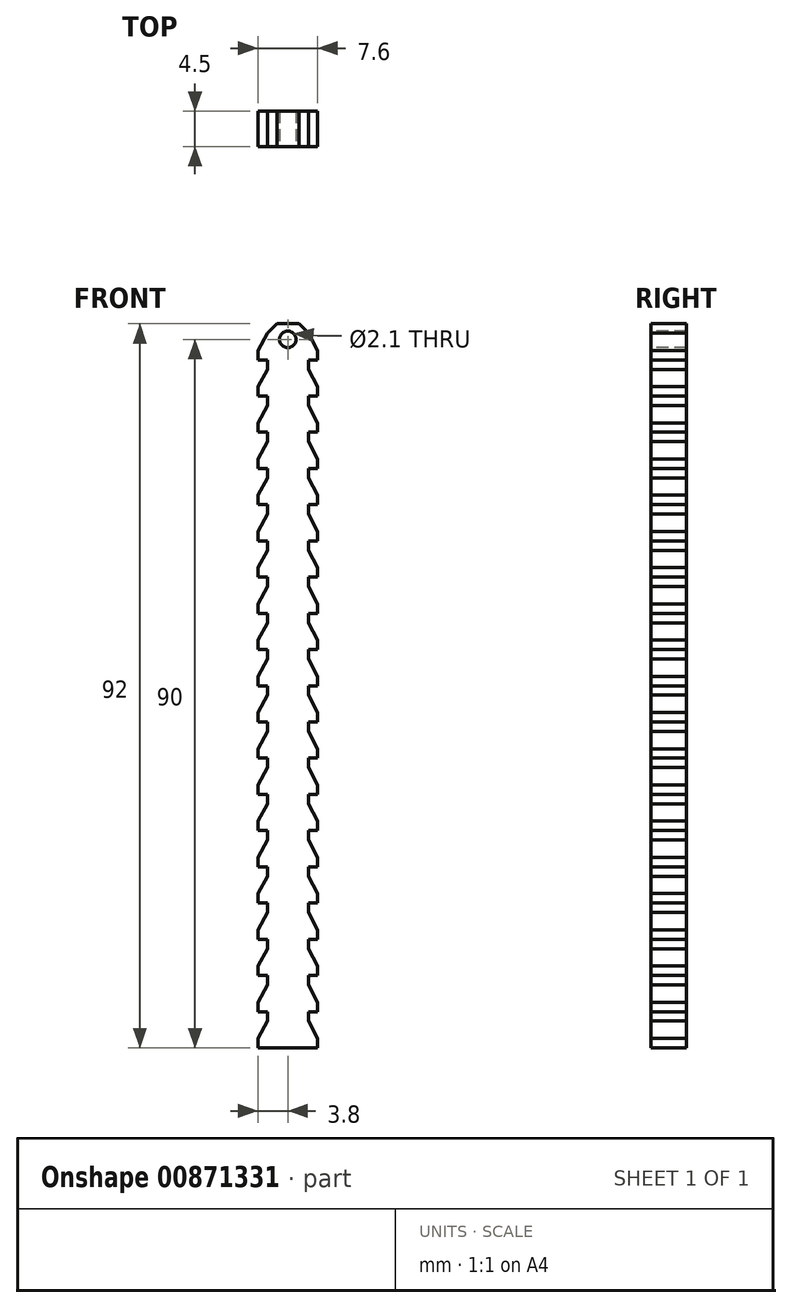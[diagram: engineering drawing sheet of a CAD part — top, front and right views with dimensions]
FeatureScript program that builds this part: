
annotation { "Feature Type Name" : "Feature", "Feature Type Description" : "" }
export const myFeature = defineFeature(function(context is Context, id is Id, definition is map)
    precondition{}
    {
        {
            var Q0;
            Q0=qCreatedBy(makeId("Front.planeOp"),FACE);
            var sketch = newSketch(context, id + "F0", { "sketchPlane" : qUnion([Q0])});
            skLineSegment(sketch, "E0", {"start": v(-3.8, 0) * mm, "end": v(-3.8, 1.2) * mm});
            skLineSegment(sketch, "E1", {"start": v(-3.8, 1.2) * mm, "end": v(-2.6, 3.4) * mm});
            skLineSegment(sketch, "E2", {"start": v(-2.6, 3.4) * mm, "end": v(-2.6, 4.6) * mm});
            skLineSegment(sketch, "E3", {"start": v(-2.6, 4.6) * mm, "end": v(-3.8, 4.6) * mm});
            skLineSegment(sketch, "E4", {"start": v(-3.8, 4.6) * mm, "end": v(-3.8, 5.8) * mm});
            skLineSegment(sketch, "E5", {"start": v(-3.8, 5.8) * mm, "end": v(-2.6, 8) * mm});
            skLineSegment(sketch, "E6", {"start": v(-3.8, 0) * mm, "end": v(-2.6, 0) * mm});
            skLineSegment(sketch, "E7.MirrorCS", {"start": v(2.6, 4.6) * mm, "end": v(3.8, 4.6) * mm});
            skLineSegment(sketch, "E8.MirrorCS", {"start": v(3.8, 4.6) * mm, "end": v(3.8, 5.8) * mm});
            skLineSegment(sketch, "E9.MirrorCS", {"start": v(2.6, 3.4) * mm, "end": v(2.6, 4.6) * mm});
            skLineSegment(sketch, "E10.MirrorCS", {"start": v(3.8, 0) * mm, "end": v(3.8, 1.2) * mm});
            skLineSegment(sketch, "E11.MirrorCS", {"start": v(3.8, 0) * mm, "end": v(2.6, 0) * mm});
            skLineSegment(sketch, "E12.MirrorCS", {"start": v(3.8, 5.8) * mm, "end": v(2.6, 8) * mm});
            skLineSegment(sketch, "E13.MirrorCS", {"start": v(3.8, 1.2) * mm, "end": v(2.6, 3.4) * mm});
            skLineSegment(sketch, "E14", {"start": v(-2.6, 8) * mm, "end": v(-2.6, 9.2) * mm});
            skLineSegment(sketch, "E15", {"start": v(2.6, 8) * mm, "end": v(2.6, 9.2) * mm});
            skLineSegment(sketch, "E16.0.1.0", {"start": v(-2.6, 12.6) * mm, "end": v(-2.6, 13.8) * mm});
            skLineSegment(sketch, "E16.0.1.1", {"start": v(-2.6, 17.2) * mm, "end": v(-2.6, 18.4) * mm});
            skLineSegment(sketch, "E16.0.1.2", {"start": v(-3.8, 10.4) * mm, "end": v(-2.6, 12.6) * mm});
            skLineSegment(sketch, "E16.0.1.3", {"start": v(2.6, 12.6) * mm, "end": v(2.6, 13.8) * mm});
            skLineSegment(sketch, "E16.0.1.4", {"start": v(2.6, 13.8) * mm, "end": v(3.8, 13.8) * mm});
            skLineSegment(sketch, "E16.0.1.5", {"start": v(2.6, 17.2) * mm, "end": v(2.6, 18.4) * mm});
            skLineSegment(sketch, "E16.0.1.6", {"start": v(-3.8, 9.2) * mm, "end": v(-2.6, 9.2) * mm});
            skLineSegment(sketch, "E16.0.1.7", {"start": v(-2.6, 13.8) * mm, "end": v(-3.8, 13.8) * mm});
            skLineSegment(sketch, "E16.0.1.8", {"start": v(-3.8, 15) * mm, "end": v(-2.6, 17.2) * mm});
            skLineSegment(sketch, "E16.0.1.9", {"start": v(-3.8, 13.8) * mm, "end": v(-3.8, 15) * mm});
            skLineSegment(sketch, "E16.0.1.10", {"start": v(3.8, 10.4) * mm, "end": v(2.6, 12.6) * mm});
            skLineSegment(sketch, "E16.0.1.11", {"start": v(3.8, 9.2) * mm, "end": v(3.8, 10.4) * mm});
            skLineSegment(sketch, "E16.0.1.12", {"start": v(-3.8, 9.2) * mm, "end": v(-3.8, 10.4) * mm});
            skLineSegment(sketch, "E16.0.1.13", {"start": v(3.8, 9.2) * mm, "end": v(2.6, 9.2) * mm});
            skLineSegment(sketch, "E16.0.1.14", {"start": v(3.8, 13.8) * mm, "end": v(3.8, 15) * mm});
            skLineSegment(sketch, "E16.0.1.15", {"start": v(3.8, 15) * mm, "end": v(2.6, 17.2) * mm});
            skLineSegment(sketch, "E16.0.2.0", {"start": v(-2.6, 21.8) * mm, "end": v(-2.6, 23) * mm});
            skLineSegment(sketch, "E16.0.2.1", {"start": v(-2.6, 26.4) * mm, "end": v(-2.6, 27.6) * mm});
            skLineSegment(sketch, "E16.0.2.2", {"start": v(-3.8, 19.6) * mm, "end": v(-2.6, 21.8) * mm});
            skLineSegment(sketch, "E16.0.2.3", {"start": v(2.6, 21.8) * mm, "end": v(2.6, 23) * mm});
            skLineSegment(sketch, "E16.0.2.4", {"start": v(2.6, 23) * mm, "end": v(3.8, 23) * mm});
            skLineSegment(sketch, "E16.0.2.5", {"start": v(2.6, 26.4) * mm, "end": v(2.6, 27.6) * mm});
            skLineSegment(sketch, "E16.0.2.6", {"start": v(-3.8, 18.4) * mm, "end": v(-2.6, 18.4) * mm});
            skLineSegment(sketch, "E16.0.2.7", {"start": v(-2.6, 23) * mm, "end": v(-3.8, 23) * mm});
            skLineSegment(sketch, "E16.0.2.8", {"start": v(-3.8, 24.2) * mm, "end": v(-2.6, 26.4) * mm});
            skLineSegment(sketch, "E16.0.2.9", {"start": v(-3.8, 23) * mm, "end": v(-3.8, 24.2) * mm});
            skLineSegment(sketch, "E16.0.2.10", {"start": v(3.8, 19.6) * mm, "end": v(2.6, 21.8) * mm});
            skLineSegment(sketch, "E16.0.2.11", {"start": v(3.8, 18.4) * mm, "end": v(3.8, 19.6) * mm});
            skLineSegment(sketch, "E16.0.2.12", {"start": v(-3.8, 18.4) * mm, "end": v(-3.8, 19.6) * mm});
            skLineSegment(sketch, "E16.0.2.13", {"start": v(3.8, 18.4) * mm, "end": v(2.6, 18.4) * mm});
            skLineSegment(sketch, "E16.0.2.14", {"start": v(3.8, 23) * mm, "end": v(3.8, 24.2) * mm});
            skLineSegment(sketch, "E16.0.2.15", {"start": v(3.8, 24.2) * mm, "end": v(2.6, 26.4) * mm});
            skLineSegment(sketch, "E16.0.3.0", {"start": v(-2.6, 31) * mm, "end": v(-2.6, 32.2) * mm});
            skLineSegment(sketch, "E16.0.3.1", {"start": v(-2.6, 35.6) * mm, "end": v(-2.6, 36.8) * mm});
            skLineSegment(sketch, "E16.0.3.2", {"start": v(-3.8, 28.8) * mm, "end": v(-2.6, 31) * mm});
            skLineSegment(sketch, "E16.0.3.3", {"start": v(2.6, 31) * mm, "end": v(2.6, 32.2) * mm});
            skLineSegment(sketch, "E16.0.3.4", {"start": v(2.6, 32.2) * mm, "end": v(3.8, 32.2) * mm});
            skLineSegment(sketch, "E16.0.3.5", {"start": v(2.6, 35.6) * mm, "end": v(2.6, 36.8) * mm});
            skLineSegment(sketch, "E16.0.3.6", {"start": v(-3.8, 27.6) * mm, "end": v(-2.6, 27.6) * mm});
            skLineSegment(sketch, "E16.0.3.7", {"start": v(-2.6, 32.2) * mm, "end": v(-3.8, 32.2) * mm});
            skLineSegment(sketch, "E16.0.3.8", {"start": v(-3.8, 33.4) * mm, "end": v(-2.6, 35.6) * mm});
            skLineSegment(sketch, "E16.0.3.9", {"start": v(-3.8, 32.2) * mm, "end": v(-3.8, 33.4) * mm});
            skLineSegment(sketch, "E16.0.3.10", {"start": v(3.8, 28.8) * mm, "end": v(2.6, 31) * mm});
            skLineSegment(sketch, "E16.0.3.11", {"start": v(3.8, 27.6) * mm, "end": v(3.8, 28.8) * mm});
            skLineSegment(sketch, "E16.0.3.12", {"start": v(-3.8, 27.6) * mm, "end": v(-3.8, 28.8) * mm});
            skLineSegment(sketch, "E16.0.3.13", {"start": v(3.8, 27.6) * mm, "end": v(2.6, 27.6) * mm});
            skLineSegment(sketch, "E16.0.3.14", {"start": v(3.8, 32.2) * mm, "end": v(3.8, 33.4) * mm});
            skLineSegment(sketch, "E16.0.3.15", {"start": v(3.8, 33.4) * mm, "end": v(2.6, 35.6) * mm});
            skLineSegment(sketch, "E16.0.4.0", {"start": v(-2.6, 40.2) * mm, "end": v(-2.6, 41.4) * mm});
            skLineSegment(sketch, "E16.0.4.1", {"start": v(-2.6, 44.8) * mm, "end": v(-2.6, 46) * mm});
            skLineSegment(sketch, "E16.0.4.2", {"start": v(-3.8, 38) * mm, "end": v(-2.6, 40.2) * mm});
            skLineSegment(sketch, "E16.0.4.3", {"start": v(2.6, 40.2) * mm, "end": v(2.6, 41.4) * mm});
            skLineSegment(sketch, "E16.0.4.4", {"start": v(2.6, 41.4) * mm, "end": v(3.8, 41.4) * mm});
            skLineSegment(sketch, "E16.0.4.5", {"start": v(2.6, 44.8) * mm, "end": v(2.6, 46) * mm});
            skLineSegment(sketch, "E16.0.4.6", {"start": v(-3.8, 36.8) * mm, "end": v(-2.6, 36.8) * mm});
            skLineSegment(sketch, "E16.0.4.7", {"start": v(-2.6, 41.4) * mm, "end": v(-3.8, 41.4) * mm});
            skLineSegment(sketch, "E16.0.4.8", {"start": v(-3.8, 42.6) * mm, "end": v(-2.6, 44.8) * mm});
            skLineSegment(sketch, "E16.0.4.9", {"start": v(-3.8, 41.4) * mm, "end": v(-3.8, 42.6) * mm});
            skLineSegment(sketch, "E16.0.4.10", {"start": v(3.8, 38) * mm, "end": v(2.6, 40.2) * mm});
            skLineSegment(sketch, "E16.0.4.11", {"start": v(3.8, 36.8) * mm, "end": v(3.8, 38) * mm});
            skLineSegment(sketch, "E16.0.4.12", {"start": v(-3.8, 36.8) * mm, "end": v(-3.8, 38) * mm});
            skLineSegment(sketch, "E16.0.4.13", {"start": v(3.8, 36.8) * mm, "end": v(2.6, 36.8) * mm});
            skLineSegment(sketch, "E16.0.4.14", {"start": v(3.8, 41.4) * mm, "end": v(3.8, 42.6) * mm});
            skLineSegment(sketch, "E16.0.4.15", {"start": v(3.8, 42.6) * mm, "end": v(2.6, 44.8) * mm});
            skLineSegment(sketch, "E16.0.5.0", {"start": v(-2.6, 49.4) * mm, "end": v(-2.6, 50.6) * mm});
            skLineSegment(sketch, "E16.0.5.1", {"start": v(-2.6, 54) * mm, "end": v(-2.6, 55.2) * mm});
            skLineSegment(sketch, "E16.0.5.2", {"start": v(-3.8, 47.2) * mm, "end": v(-2.6, 49.4) * mm});
            skLineSegment(sketch, "E16.0.5.3", {"start": v(2.6, 49.4) * mm, "end": v(2.6, 50.6) * mm});
            skLineSegment(sketch, "E16.0.5.4", {"start": v(2.6, 50.6) * mm, "end": v(3.8, 50.6) * mm});
            skLineSegment(sketch, "E16.0.5.5", {"start": v(2.6, 54) * mm, "end": v(2.6, 55.2) * mm});
            skLineSegment(sketch, "E16.0.5.6", {"start": v(-3.8, 46) * mm, "end": v(-2.6, 46) * mm});
            skLineSegment(sketch, "E16.0.5.7", {"start": v(-2.6, 50.6) * mm, "end": v(-3.8, 50.6) * mm});
            skLineSegment(sketch, "E16.0.5.8", {"start": v(-3.8, 51.8) * mm, "end": v(-2.6, 54) * mm});
            skLineSegment(sketch, "E16.0.5.9", {"start": v(-3.8, 50.6) * mm, "end": v(-3.8, 51.8) * mm});
            skLineSegment(sketch, "E16.0.5.10", {"start": v(3.8, 47.2) * mm, "end": v(2.6, 49.4) * mm});
            skLineSegment(sketch, "E16.0.5.11", {"start": v(3.8, 46) * mm, "end": v(3.8, 47.2) * mm});
            skLineSegment(sketch, "E16.0.5.12", {"start": v(-3.8, 46) * mm, "end": v(-3.8, 47.2) * mm});
            skLineSegment(sketch, "E16.0.5.13", {"start": v(3.8, 46) * mm, "end": v(2.6, 46) * mm});
            skLineSegment(sketch, "E16.0.5.14", {"start": v(3.8, 50.6) * mm, "end": v(3.8, 51.8) * mm});
            skLineSegment(sketch, "E16.0.5.15", {"start": v(3.8, 51.8) * mm, "end": v(2.6, 54) * mm});
            skLineSegment(sketch, "E16.0.6.0", {"start": v(-2.6, 58.6) * mm, "end": v(-2.6, 59.8) * mm});
            skLineSegment(sketch, "E16.0.6.1", {"start": v(-2.6, 63.2) * mm, "end": v(-2.6, 64.4) * mm});
            skLineSegment(sketch, "E16.0.6.2", {"start": v(-3.8, 56.4) * mm, "end": v(-2.6, 58.6) * mm});
            skLineSegment(sketch, "E16.0.6.3", {"start": v(2.6, 58.6) * mm, "end": v(2.6, 59.8) * mm});
            skLineSegment(sketch, "E16.0.6.4", {"start": v(2.6, 59.8) * mm, "end": v(3.8, 59.8) * mm});
            skLineSegment(sketch, "E16.0.6.5", {"start": v(2.6, 63.2) * mm, "end": v(2.6, 64.4) * mm});
            skLineSegment(sketch, "E16.0.6.6", {"start": v(-3.8, 55.2) * mm, "end": v(-2.6, 55.2) * mm});
            skLineSegment(sketch, "E16.0.6.7", {"start": v(-2.6, 59.8) * mm, "end": v(-3.8, 59.8) * mm});
            skLineSegment(sketch, "E16.0.6.8", {"start": v(-3.8, 61) * mm, "end": v(-2.6, 63.2) * mm});
            skLineSegment(sketch, "E16.0.6.9", {"start": v(-3.8, 59.8) * mm, "end": v(-3.8, 61) * mm});
            skLineSegment(sketch, "E16.0.6.10", {"start": v(3.8, 56.4) * mm, "end": v(2.6, 58.6) * mm});
            skLineSegment(sketch, "E16.0.6.11", {"start": v(3.8, 55.2) * mm, "end": v(3.8, 56.4) * mm});
            skLineSegment(sketch, "E16.0.6.12", {"start": v(-3.8, 55.2) * mm, "end": v(-3.8, 56.4) * mm});
            skLineSegment(sketch, "E16.0.6.13", {"start": v(3.8, 55.2) * mm, "end": v(2.6, 55.2) * mm});
            skLineSegment(sketch, "E16.0.6.14", {"start": v(3.8, 59.8) * mm, "end": v(3.8, 61) * mm});
            skLineSegment(sketch, "E16.0.6.15", {"start": v(3.8, 61) * mm, "end": v(2.6, 63.2) * mm});
            skLineSegment(sketch, "E16.0.7.0", {"start": v(-2.6, 67.8) * mm, "end": v(-2.6, 69) * mm});
            skLineSegment(sketch, "E16.0.7.1", {"start": v(-2.6, 72.4) * mm, "end": v(-2.6, 73.6) * mm});
            skLineSegment(sketch, "E16.0.7.2", {"start": v(-3.8, 65.6) * mm, "end": v(-2.6, 67.8) * mm});
            skLineSegment(sketch, "E16.0.7.3", {"start": v(2.6, 67.8) * mm, "end": v(2.6, 69) * mm});
            skLineSegment(sketch, "E16.0.7.4", {"start": v(2.6, 69) * mm, "end": v(3.8, 69) * mm});
            skLineSegment(sketch, "E16.0.7.5", {"start": v(2.6, 72.4) * mm, "end": v(2.6, 73.6) * mm});
            skLineSegment(sketch, "E16.0.7.6", {"start": v(-3.8, 64.4) * mm, "end": v(-2.6, 64.4) * mm});
            skLineSegment(sketch, "E16.0.7.7", {"start": v(-2.6, 69) * mm, "end": v(-3.8, 69) * mm});
            skLineSegment(sketch, "E16.0.7.8", {"start": v(-3.8, 70.2) * mm, "end": v(-2.6, 72.4) * mm});
            skLineSegment(sketch, "E16.0.7.9", {"start": v(-3.8, 69) * mm, "end": v(-3.8, 70.2) * mm});
            skLineSegment(sketch, "E16.0.7.10", {"start": v(3.8, 65.6) * mm, "end": v(2.6, 67.8) * mm});
            skLineSegment(sketch, "E16.0.7.11", {"start": v(3.8, 64.4) * mm, "end": v(3.8, 65.6) * mm});
            skLineSegment(sketch, "E16.0.7.12", {"start": v(-3.8, 64.4) * mm, "end": v(-3.8, 65.6) * mm});
            skLineSegment(sketch, "E16.0.7.13", {"start": v(3.8, 64.4) * mm, "end": v(2.6, 64.4) * mm});
            skLineSegment(sketch, "E16.0.7.14", {"start": v(3.8, 69) * mm, "end": v(3.8, 70.2) * mm});
            skLineSegment(sketch, "E16.0.7.15", {"start": v(3.8, 70.2) * mm, "end": v(2.6, 72.4) * mm});
            skLineSegment(sketch, "E16.0.8.0", {"start": v(-2.6, 77) * mm, "end": v(-2.6, 78.2) * mm});
            skLineSegment(sketch, "E16.0.8.1", {"start": v(-2.6, 81.6) * mm, "end": v(-2.6, 82.8) * mm});
            skLineSegment(sketch, "E16.0.8.2", {"start": v(-3.8, 74.8) * mm, "end": v(-2.6, 77) * mm});
            skLineSegment(sketch, "E16.0.8.3", {"start": v(2.6, 77) * mm, "end": v(2.6, 78.2) * mm});
            skLineSegment(sketch, "E16.0.8.4", {"start": v(2.6, 78.2) * mm, "end": v(3.8, 78.2) * mm});
            skLineSegment(sketch, "E16.0.8.5", {"start": v(2.6, 81.6) * mm, "end": v(2.6, 82.8) * mm});
            skLineSegment(sketch, "E16.0.8.6", {"start": v(-3.8, 73.6) * mm, "end": v(-2.6, 73.6) * mm});
            skLineSegment(sketch, "E16.0.8.7", {"start": v(-2.6, 78.2) * mm, "end": v(-3.8, 78.2) * mm});
            skLineSegment(sketch, "E16.0.8.8", {"start": v(-3.8, 79.4) * mm, "end": v(-2.6, 81.6) * mm});
            skLineSegment(sketch, "E16.0.8.9", {"start": v(-3.8, 78.2) * mm, "end": v(-3.8, 79.4) * mm});
            skLineSegment(sketch, "E16.0.8.10", {"start": v(3.8, 74.8) * mm, "end": v(2.6, 77) * mm});
            skLineSegment(sketch, "E16.0.8.11", {"start": v(3.8, 73.6) * mm, "end": v(3.8, 74.8) * mm});
            skLineSegment(sketch, "E16.0.8.12", {"start": v(-3.8, 73.6) * mm, "end": v(-3.8, 74.8) * mm});
            skLineSegment(sketch, "E16.0.8.13", {"start": v(3.8, 73.6) * mm, "end": v(2.6, 73.6) * mm});
            skLineSegment(sketch, "E16.0.8.14", {"start": v(3.8, 78.2) * mm, "end": v(3.8, 79.4) * mm});
            skLineSegment(sketch, "E16.0.8.15", {"start": v(3.8, 79.4) * mm, "end": v(2.6, 81.6) * mm});
            skLineSegment(sketch, "E16.0.9.0", {"start": v(-2.6, 86.2) * mm, "end": v(-2.6, 87.4) * mm});
            skLineSegment(sketch, "E16.0.9.1", {"start": v(-2.6, 90.8) * mm, "end": v(-2.6, 92) * mm});
            skLineSegment(sketch, "E16.0.9.2", {"start": v(-3.8, 84) * mm, "end": v(-2.6, 86.2) * mm});
            skLineSegment(sketch, "E16.0.9.3", {"start": v(2.6, 86.2) * mm, "end": v(2.6, 87.4) * mm});
            skLineSegment(sketch, "E16.0.9.4", {"start": v(2.6, 87.4) * mm, "end": v(3.8, 87.4) * mm});
            skLineSegment(sketch, "E16.0.9.5", {"start": v(2.6, 90.8) * mm, "end": v(2.6, 92) * mm});
            skLineSegment(sketch, "E16.0.9.6", {"start": v(-3.8, 82.8) * mm, "end": v(-2.6, 82.8) * mm});
            skLineSegment(sketch, "E16.0.9.7", {"start": v(-2.6, 87.4) * mm, "end": v(-3.8, 87.4) * mm});
            skLineSegment(sketch, "E16.0.9.8", {"start": v(-3.8, 88.6) * mm, "end": v(-2.6, 90.8) * mm});
            skLineSegment(sketch, "E16.0.9.9", {"start": v(-3.8, 87.4) * mm, "end": v(-3.8, 88.6) * mm});
            skLineSegment(sketch, "E16.0.9.10", {"start": v(3.8, 84) * mm, "end": v(2.6, 86.2) * mm});
            skLineSegment(sketch, "E16.0.9.11", {"start": v(3.8, 82.8) * mm, "end": v(3.8, 84) * mm});
            skLineSegment(sketch, "E16.0.9.12", {"start": v(-3.8, 82.8) * mm, "end": v(-3.8, 84) * mm});
            skLineSegment(sketch, "E16.0.9.13", {"start": v(3.8, 82.8) * mm, "end": v(2.6, 82.8) * mm});
            skLineSegment(sketch, "E16.0.9.14", {"start": v(3.8, 87.4) * mm, "end": v(3.8, 88.6) * mm});
            skLineSegment(sketch, "E16.0.9.15", {"start": v(3.8, 88.6) * mm, "end": v(2.6, 90.8) * mm});
            skLineSegment(sketch, "E16.direction1", {"start": v(-3.8, 0) * mm, "end": v(21, 0) * mm, "construction": true});
            skLineSegment(sketch, "E16.direction2", {"start": v(-3.8, 0) * mm, "end": v(-3.8, 9.2) * mm, "construction": true});
            skLineSegment(sketch, "E17", {"start": v(-2.6, 0) * mm, "end": v(2.6, 0) * mm});
            skLineSegment(sketch, "E18", {"start": v(-2.6, 92) * mm, "end": v(2.6, 92) * mm});
            skSolve(sketch);
        }
        {
            var Q0;
            Q0=makeQuery(id+"F0.imprint","IMPRINT",FACE,{"disambiguationData":[TD([[makeQuery(id+"F0.imprint","IMPRINT",EDGE,{"derivedFrom":sQuery(id+"F0.wireOp",EDGE,"E0")}),-1.0]])]});
            extrude(context, id + "F1", {"entities" : qUnion([Q0]), "depth" : 4.5 * mm, "offsetDistance" : 25 * mm});
        }
        {
            var Q0;
            Q0=makeQuery(id+"F1.opExtrude","SWEPT_EDGE",EDGE,{"disambiguationData":[OSD([sQuery(id+"F0.wireOp",EDGE,"E16.0.9.5"),sQuery(id+"F0.wireOp",EDGE,"E18")])]});
            var Q1;
            Q1=makeQuery(id+"F1.opExtrude","SWEPT_EDGE",EDGE,{"disambiguationData":[OSD([sQuery(id+"F0.wireOp",EDGE,"E16.0.9.1"),sQuery(id+"F0.wireOp",EDGE,"E18")])]});
            chamfer(context, id + "F2", {"entities" : qUnion([Q0, Q1]), "width" : 1.2 * mm, "tangentPropagation" : true});
        }
        {
            var Q0;
            Q0=makeQuery(id+"F1.opExtrude","CAP_FACE",FACE,{"disambiguationData":[OSD([sQuery(id+"F0.wireOp",EDGE,"E0"),sQuery(id+"F0.wireOp",EDGE,"E1"),sQuery(id+"F0.wireOp",EDGE,"E2"),sQuery(id+"F0.wireOp",EDGE,"E3"),sQuery(id+"F0.wireOp",EDGE,"E4"),sQuery(id+"F0.wireOp",EDGE,"E5"),sQuery(id+"F0.wireOp",EDGE,"E6"),sQuery(id+"F0.wireOp",EDGE,"E7.MirrorCS"),sQuery(id+"F0.wireOp",EDGE,"E8.MirrorCS"),sQuery(id+"F0.wireOp",EDGE,"E9.MirrorCS"),sQuery(id+"F0.wireOp",EDGE,"E10.MirrorCS"),sQuery(id+"F0.wireOp",EDGE,"E11.MirrorCS"),sQuery(id+"F0.wireOp",EDGE,"E12.MirrorCS"),sQuery(id+"F0.wireOp",EDGE,"E13.MirrorCS"),sQuery(id+"F0.wireOp",EDGE,"E14"),sQuery(id+"F0.wireOp",EDGE,"E15"),sQuery(id+"F0.wireOp",EDGE,"E16.0.1.0"),sQuery(id+"F0.wireOp",EDGE,"E16.0.1.1"),sQuery(id+"F0.wireOp",EDGE,"E16.0.1.2"),sQuery(id+"F0.wireOp",EDGE,"E16.0.1.3"),sQuery(id+"F0.wireOp",EDGE,"E16.0.1.4"),sQuery(id+"F0.wireOp",EDGE,"E16.0.1.5"),sQuery(id+"F0.wireOp",EDGE,"E16.0.1.6"),sQuery(id+"F0.wireOp",EDGE,"E16.0.1.7"),sQuery(id+"F0.wireOp",EDGE,"E16.0.1.8"),sQuery(id+"F0.wireOp",EDGE,"E16.0.1.9"),sQuery(id+"F0.wireOp",EDGE,"E16.0.1.10"),sQuery(id+"F0.wireOp",EDGE,"E16.0.1.11"),sQuery(id+"F0.wireOp",EDGE,"E16.0.1.12"),sQuery(id+"F0.wireOp",EDGE,"E16.0.1.13"),sQuery(id+"F0.wireOp",EDGE,"E16.0.1.14"),sQuery(id+"F0.wireOp",EDGE,"E16.0.1.15"),sQuery(id+"F0.wireOp",EDGE,"E16.0.2.0"),sQuery(id+"F0.wireOp",EDGE,"E16.0.2.1"),sQuery(id+"F0.wireOp",EDGE,"E16.0.2.2"),sQuery(id+"F0.wireOp",EDGE,"E16.0.2.3"),sQuery(id+"F0.wireOp",EDGE,"E16.0.2.4"),sQuery(id+"F0.wireOp",EDGE,"E16.0.2.5"),sQuery(id+"F0.wireOp",EDGE,"E16.0.2.6"),sQuery(id+"F0.wireOp",EDGE,"E16.0.2.7"),sQuery(id+"F0.wireOp",EDGE,"E16.0.2.8"),sQuery(id+"F0.wireOp",EDGE,"E16.0.2.9"),sQuery(id+"F0.wireOp",EDGE,"E16.0.2.10"),sQuery(id+"F0.wireOp",EDGE,"E16.0.2.11"),sQuery(id+"F0.wireOp",EDGE,"E16.0.2.12"),sQuery(id+"F0.wireOp",EDGE,"E16.0.2.13"),sQuery(id+"F0.wireOp",EDGE,"E16.0.2.14"),sQuery(id+"F0.wireOp",EDGE,"E16.0.2.15"),sQuery(id+"F0.wireOp",EDGE,"E16.0.3.0"),sQuery(id+"F0.wireOp",EDGE,"E16.0.3.1"),sQuery(id+"F0.wireOp",EDGE,"E16.0.3.2"),sQuery(id+"F0.wireOp",EDGE,"E16.0.3.3"),sQuery(id+"F0.wireOp",EDGE,"E16.0.3.4"),sQuery(id+"F0.wireOp",EDGE,"E16.0.3.5"),sQuery(id+"F0.wireOp",EDGE,"E16.0.3.6"),sQuery(id+"F0.wireOp",EDGE,"E16.0.3.7"),sQuery(id+"F0.wireOp",EDGE,"E16.0.3.8"),sQuery(id+"F0.wireOp",EDGE,"E16.0.3.9"),sQuery(id+"F0.wireOp",EDGE,"E16.0.3.10"),sQuery(id+"F0.wireOp",EDGE,"E16.0.3.11"),sQuery(id+"F0.wireOp",EDGE,"E16.0.3.12"),sQuery(id+"F0.wireOp",EDGE,"E16.0.3.13"),sQuery(id+"F0.wireOp",EDGE,"E16.0.3.14"),sQuery(id+"F0.wireOp",EDGE,"E16.0.3.15"),sQuery(id+"F0.wireOp",EDGE,"E16.0.4.0"),sQuery(id+"F0.wireOp",EDGE,"E16.0.4.1"),sQuery(id+"F0.wireOp",EDGE,"E16.0.4.2"),sQuery(id+"F0.wireOp",EDGE,"E16.0.4.3"),sQuery(id+"F0.wireOp",EDGE,"E16.0.4.4"),sQuery(id+"F0.wireOp",EDGE,"E16.0.4.5"),sQuery(id+"F0.wireOp",EDGE,"E16.0.4.6"),sQuery(id+"F0.wireOp",EDGE,"E16.0.4.7"),sQuery(id+"F0.wireOp",EDGE,"E16.0.4.8"),sQuery(id+"F0.wireOp",EDGE,"E16.0.4.9"),sQuery(id+"F0.wireOp",EDGE,"E16.0.4.10"),sQuery(id+"F0.wireOp",EDGE,"E16.0.4.11"),sQuery(id+"F0.wireOp",EDGE,"E16.0.4.12"),sQuery(id+"F0.wireOp",EDGE,"E16.0.4.13"),sQuery(id+"F0.wireOp",EDGE,"E16.0.4.14"),sQuery(id+"F0.wireOp",EDGE,"E16.0.4.15"),sQuery(id+"F0.wireOp",EDGE,"E16.0.5.0"),sQuery(id+"F0.wireOp",EDGE,"E16.0.5.1"),sQuery(id+"F0.wireOp",EDGE,"E16.0.5.2"),sQuery(id+"F0.wireOp",EDGE,"E16.0.5.3"),sQuery(id+"F0.wireOp",EDGE,"E16.0.5.4"),sQuery(id+"F0.wireOp",EDGE,"E16.0.5.5"),sQuery(id+"F0.wireOp",EDGE,"E16.0.5.6"),sQuery(id+"F0.wireOp",EDGE,"E16.0.5.7"),sQuery(id+"F0.wireOp",EDGE,"E16.0.5.8"),sQuery(id+"F0.wireOp",EDGE,"E16.0.5.9"),sQuery(id+"F0.wireOp",EDGE,"E16.0.5.10"),sQuery(id+"F0.wireOp",EDGE,"E16.0.5.11"),sQuery(id+"F0.wireOp",EDGE,"E16.0.5.12"),sQuery(id+"F0.wireOp",EDGE,"E16.0.5.13"),sQuery(id+"F0.wireOp",EDGE,"E16.0.5.14"),sQuery(id+"F0.wireOp",EDGE,"E16.0.5.15"),sQuery(id+"F0.wireOp",EDGE,"E16.0.6.0"),sQuery(id+"F0.wireOp",EDGE,"E16.0.6.1"),sQuery(id+"F0.wireOp",EDGE,"E16.0.6.2"),sQuery(id+"F0.wireOp",EDGE,"E16.0.6.3"),sQuery(id+"F0.wireOp",EDGE,"E16.0.6.4"),sQuery(id+"F0.wireOp",EDGE,"E16.0.6.5"),sQuery(id+"F0.wireOp",EDGE,"E16.0.6.6"),sQuery(id+"F0.wireOp",EDGE,"E16.0.6.7"),sQuery(id+"F0.wireOp",EDGE,"E16.0.6.8"),sQuery(id+"F0.wireOp",EDGE,"E16.0.6.9"),sQuery(id+"F0.wireOp",EDGE,"E16.0.6.10"),sQuery(id+"F0.wireOp",EDGE,"E16.0.6.11"),sQuery(id+"F0.wireOp",EDGE,"E16.0.6.12"),sQuery(id+"F0.wireOp",EDGE,"E16.0.6.13"),sQuery(id+"F0.wireOp",EDGE,"E16.0.6.14"),sQuery(id+"F0.wireOp",EDGE,"E16.0.6.15"),sQuery(id+"F0.wireOp",EDGE,"E16.0.7.0"),sQuery(id+"F0.wireOp",EDGE,"E16.0.7.1"),sQuery(id+"F0.wireOp",EDGE,"E16.0.7.2"),sQuery(id+"F0.wireOp",EDGE,"E16.0.7.3"),sQuery(id+"F0.wireOp",EDGE,"E16.0.7.4"),sQuery(id+"F0.wireOp",EDGE,"E16.0.7.5"),sQuery(id+"F0.wireOp",EDGE,"E16.0.7.6"),sQuery(id+"F0.wireOp",EDGE,"E16.0.7.7"),sQuery(id+"F0.wireOp",EDGE,"E16.0.7.8"),sQuery(id+"F0.wireOp",EDGE,"E16.0.7.9"),sQuery(id+"F0.wireOp",EDGE,"E16.0.7.10"),sQuery(id+"F0.wireOp",EDGE,"E16.0.7.11"),sQuery(id+"F0.wireOp",EDGE,"E16.0.7.12"),sQuery(id+"F0.wireOp",EDGE,"E16.0.7.13"),sQuery(id+"F0.wireOp",EDGE,"E16.0.7.14"),sQuery(id+"F0.wireOp",EDGE,"E16.0.7.15"),sQuery(id+"F0.wireOp",EDGE,"E16.0.8.0"),sQuery(id+"F0.wireOp",EDGE,"E16.0.8.1"),sQuery(id+"F0.wireOp",EDGE,"E16.0.8.2"),sQuery(id+"F0.wireOp",EDGE,"E16.0.8.3"),sQuery(id+"F0.wireOp",EDGE,"E16.0.8.4"),sQuery(id+"F0.wireOp",EDGE,"E16.0.8.5"),sQuery(id+"F0.wireOp",EDGE,"E16.0.8.6"),sQuery(id+"F0.wireOp",EDGE,"E16.0.8.7"),sQuery(id+"F0.wireOp",EDGE,"E16.0.8.8"),sQuery(id+"F0.wireOp",EDGE,"E16.0.8.9"),sQuery(id+"F0.wireOp",EDGE,"E16.0.8.10"),sQuery(id+"F0.wireOp",EDGE,"E16.0.8.11"),sQuery(id+"F0.wireOp",EDGE,"E16.0.8.12"),sQuery(id+"F0.wireOp",EDGE,"E16.0.8.13"),sQuery(id+"F0.wireOp",EDGE,"E16.0.8.14"),sQuery(id+"F0.wireOp",EDGE,"E16.0.8.15"),sQuery(id+"F0.wireOp",EDGE,"E16.0.9.0"),sQuery(id+"F0.wireOp",EDGE,"E16.0.9.1"),sQuery(id+"F0.wireOp",EDGE,"E16.0.9.2"),sQuery(id+"F0.wireOp",EDGE,"E16.0.9.3"),sQuery(id+"F0.wireOp",EDGE,"E16.0.9.4"),sQuery(id+"F0.wireOp",EDGE,"E16.0.9.5"),sQuery(id+"F0.wireOp",EDGE,"E16.0.9.6"),sQuery(id+"F0.wireOp",EDGE,"E16.0.9.7"),sQuery(id+"F0.wireOp",EDGE,"E16.0.9.8"),sQuery(id+"F0.wireOp",EDGE,"E16.0.9.9"),sQuery(id+"F0.wireOp",EDGE,"E16.0.9.10"),sQuery(id+"F0.wireOp",EDGE,"E16.0.9.11"),sQuery(id+"F0.wireOp",EDGE,"E16.0.9.12"),sQuery(id+"F0.wireOp",EDGE,"E16.0.9.13"),sQuery(id+"F0.wireOp",EDGE,"E16.0.9.14"),sQuery(id+"F0.wireOp",EDGE,"E16.0.9.15"),sQuery(id+"F0.wireOp",EDGE,"E17"),sQuery(id+"F0.wireOp",EDGE,"E18")])],"isStart":false});
            var sketch = newSketch(context, id + "F3", { "sketchPlane" : qUnion([Q0])});
            skCircle(sketch, "E19", {"center": v(0, 28.3) * mm, "radius": 0.5 * mm});
            skCircle(sketch, "E20", {"center": v(0, 90) * mm, "radius": 1.05 * mm});
            skSolve(sketch);
        }
        {
            var Q0;
            Q0=makeQuery(id+"F3.imprint","IMPRINT",FACE,{"disambiguationData":[TD([[makeQuery(id+"F3.imprint","IMPRINT",EDGE,{"derivedFrom":sQuery(id+"F3.wireOp",EDGE,"E20")}),1.0]])]});
            extrude(context, id + "F4", {"entities" : qUnion([Q0]), "operationType" : NewBodyOperationType.REMOVE, "oppositeDirection" : true, "depth" : 25 * mm, "offsetDistance" : 25 * mm});
        }
    });
